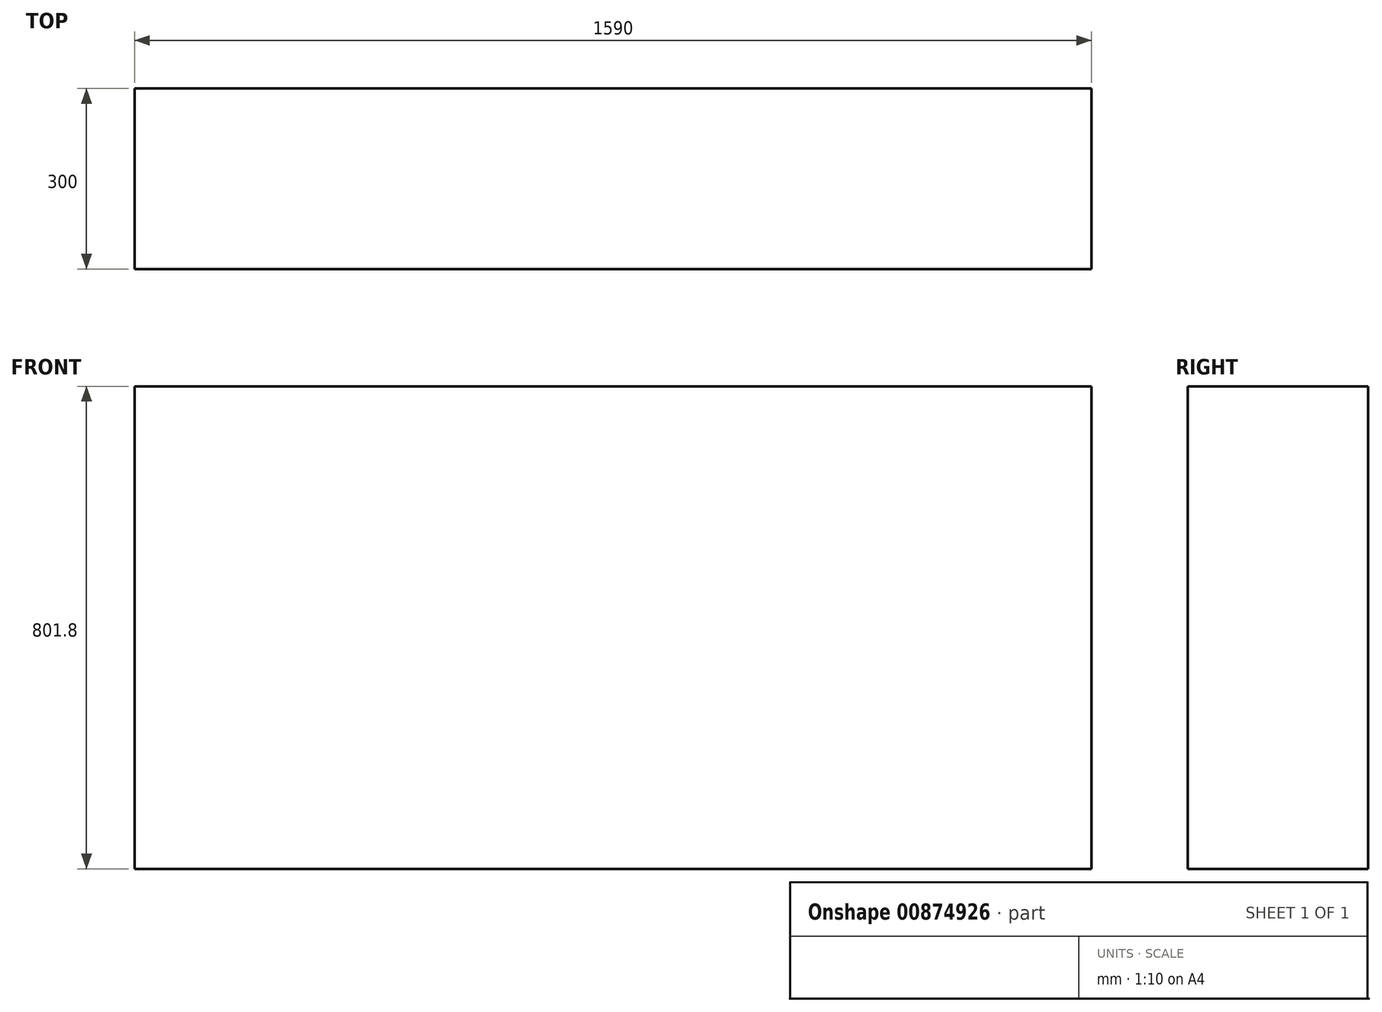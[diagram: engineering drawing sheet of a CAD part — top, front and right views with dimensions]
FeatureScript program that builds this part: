
annotation { "Feature Type Name" : "Feature", "Feature Type Description" : "" }
export const myFeature = defineFeature(function(context is Context, id is Id, definition is map)
    precondition{}
    {
        {
            var Q0;
            Q0=qCreatedBy(makeId("Top.planeOp"),FACE);
            var sketch = newSketch(context, id + "F0", { "sketchPlane" : qUnion([Q0])});
            skLineSegment(sketch, "E0.bottom", {"start": v(0, 0) * mm, "end": v(1590, 0) * mm});
            skLineSegment(sketch, "E0.top", {"start": v(0, 300) * mm, "end": v(1590, 300) * mm});
            skLineSegment(sketch, "E0.left", {"start": v(0, 0) * mm, "end": v(0, 300) * mm});
            skLineSegment(sketch, "E0.right", {"start": v(1590, 0) * mm, "end": v(1590, 300) * mm});
            skSolve(sketch);
        }
        {
            var Q0;
            Q0=qSketchRegion(id+"F0",true);
            extrude(context, id + "F1", {"entities" : qUnion([Q0]), "depth" : 50.8 * mm + 751 * mm, "offsetDistance" : 25 * mm});
        }
    });
